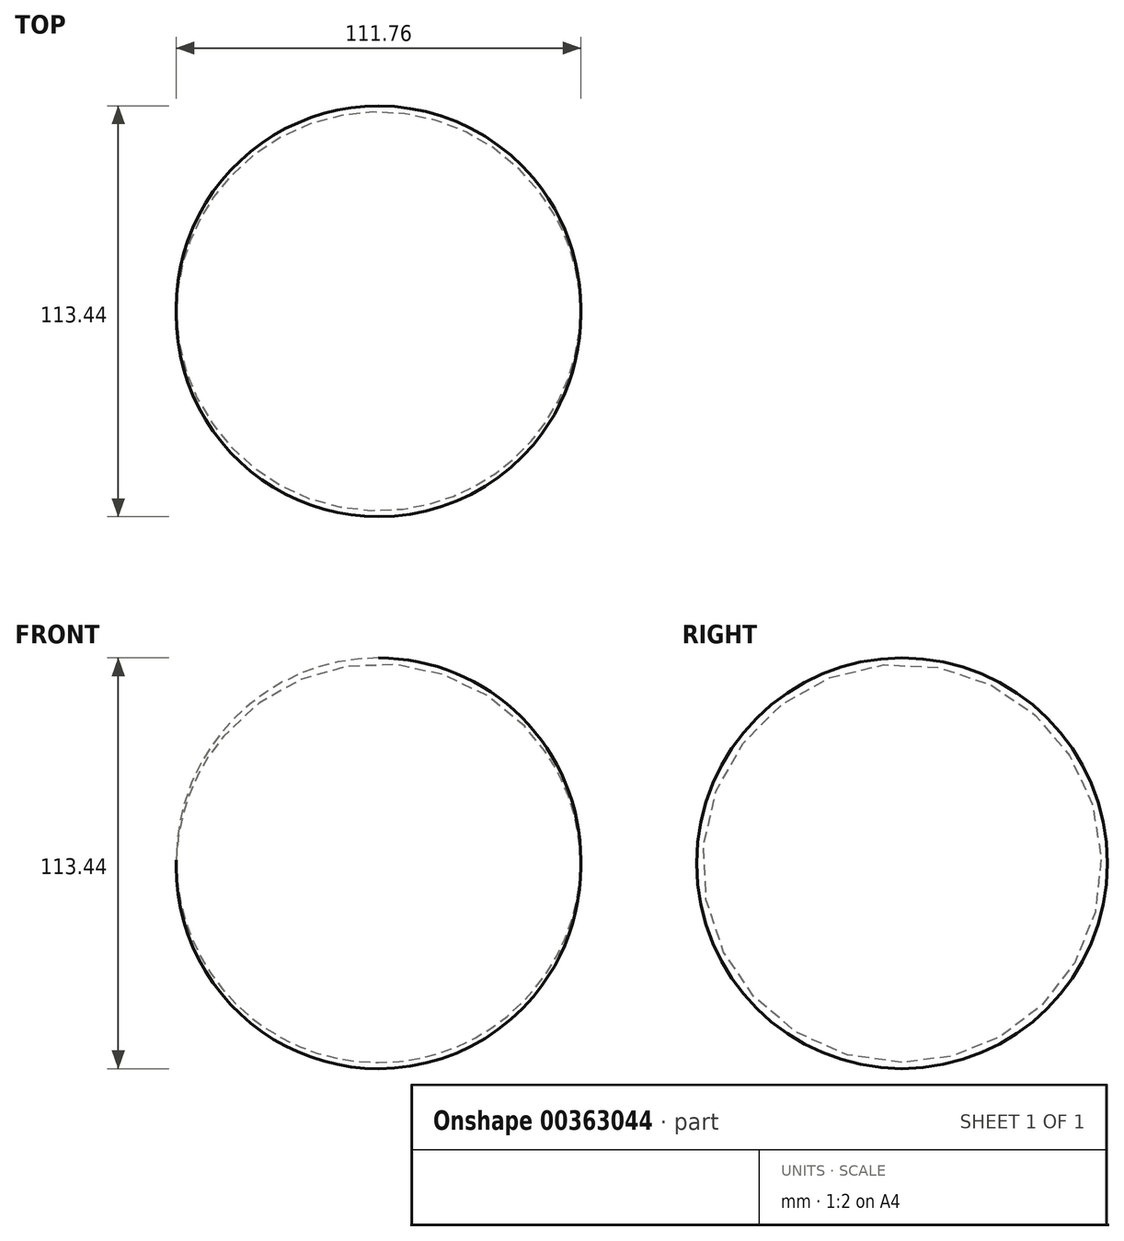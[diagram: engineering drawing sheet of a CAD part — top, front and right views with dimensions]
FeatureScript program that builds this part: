
annotation { "Feature Type Name" : "Feature", "Feature Type Description" : "" }
export const myFeature = defineFeature(function(context is Context, id is Id, definition is map)
    precondition{}
    {
        {
            var Q0;
            Q0=qCreatedBy(makeId("Front.planeOp"),FACE);
            var sketch = newSketch(context, id + "F0", { "sketchPlane" : qUnion([Q0])});
            skLineSegment(sketch, "E0", {"start": v(-64.75, 0) * mm, "end": v(47, 0) * mm});
            skArc(sketch, "E1", {"start": v(-64.75, 0) * mm, "mid": v(-8.87, -55.04) * mm, "end": v(47, 0) * mm});
            skSolve(sketch);
        }
        {
            var Q0;
            Q0=makeQuery(id+"F0.imprint","IMPRINT",FACE,{"disambiguationData":[TD([[makeQuery(id+"F0.imprint","IMPRINT",EDGE,{"derivedFrom":sQuery(id+"F0.wireOp",EDGE,"E0")}),-1.0]])]});
            var Q1;
            Q1=sQuery(id+"F0.wireOp",EDGE,"E0");
            revolve(context, id + "F1", {"entities" : qUnion([Q0]), "axis" : qUnion([Q1]), "revolveType" : RevolveType.FULL});
        }
    });
